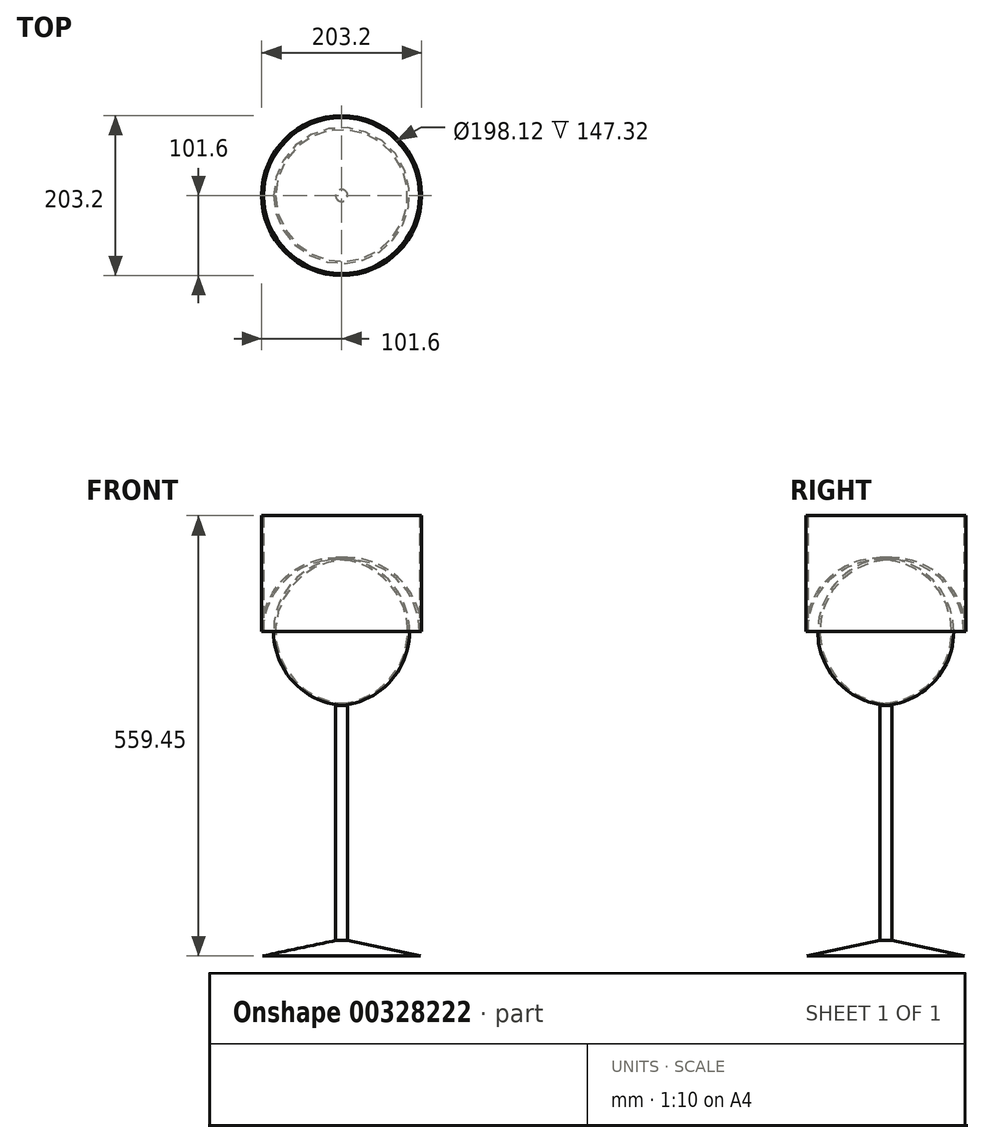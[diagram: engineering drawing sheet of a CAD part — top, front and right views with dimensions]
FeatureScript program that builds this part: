
annotation { "Feature Type Name" : "Feature", "Feature Type Description" : "" }
export const myFeature = defineFeature(function(context is Context, id is Id, definition is map)
    precondition{}
    {
        {
            var Q0;
            Q0=qCreatedBy(makeId("Top.planeOp"),FACE);
            var sketch = newSketch(context, id + "F0", { "sketchPlane" : qUnion([Q0])});
            skCircle(sketch, "E0", {"center": v(0, 0) * mm, "radius": 101.6 * mm});
            skSolve(sketch);
        }
        {
            var Q0;
            Q0=makeQuery(id+"F0.imprint","IMPRINT",FACE,{"disambiguationData":[TD([[makeQuery(id+"F0.imprint","IMPRINT",EDGE,{"derivedFrom":sQuery(id+"F0.wireOp",EDGE,"E0")}),1.0]])]});
            extrude(context, id + "F1", {"entities" : qUnion([Q0]), "depth" : 241.3 * mm});
        }
        {
            var Q0;
            Q0=makeQuery(id+"F1.opExtrude","CAP_EDGE",EDGE,{"disambiguationData":[OSD([sQuery(id+"F0.wireOp",EDGE,"E0")])],"isStart":true});
            fillet(context, id + "F2", {"entities" : qUnion([Q0]), "radius" : 93.98 * mm, "tangentPropagation" : true, "allowEdgeOverflow" : false});
        }
        {
            var Q0;
            Q0=makeQuery(id+"F1.opExtrude","CAP_FACE",FACE,{"disambiguationData":[OSD([sQuery(id+"F0.wireOp",EDGE,"E0")])],"isStart":true});
            extrude(context, id + "F3", {"entities" : qUnion([Q0]), "depth" : 304.8 * mm});
        }
        {
            var Q0;
            Q0=qCreatedBy(makeId("Front.planeOp"),FACE);
            var sketch = newSketch(context, id + "F4", { "sketchPlane" : qUnion([Q0])});
            skLineSegment(sketch, "E1", {"start": v(0, -296.89) * mm, "end": v(100.12, -318.15) * mm});
            skLineSegment(sketch, "E2", {"start": v(100.12, -318.15) * mm, "end": v(0, -318.15) * mm});
            skLineSegment(sketch, "E3", {"start": v(0, -318.15) * mm, "end": v(0, -296.89) * mm});
            skSolve(sketch);
        }
        {
            var Q0;
            Q0=makeQuery(id+"F4.imprint","IMPRINT",FACE,{"disambiguationData":[TD([[makeQuery(id+"F4.imprint","IMPRINT",EDGE,{"derivedFrom":sQuery(id+"F4.wireOp",EDGE,"E1")}),-1.0]])]});
            var Q1;
            Q1=sQuery(id+"F4.wireOp",EDGE,"E3");
            revolve(context, id + "F5", {"operationType" : NewBodyOperationType.ADD, "entities" : qUnion([Q0]), "axis" : qUnion([Q1]), "revolveType" : RevolveType.FULL});
        }
        {
            var Q0;
            Q0=makeQuery(id+"F1.opExtrude","CAP_FACE",FACE,{"disambiguationData":[OSD([sQuery(id+"F0.wireOp",EDGE,"E0")])],"isStart":false});
            shell(context, id + "F6", {"entities" : qUnion([Q0]), "thickness" : 2.54 * mm});
        }
    });
